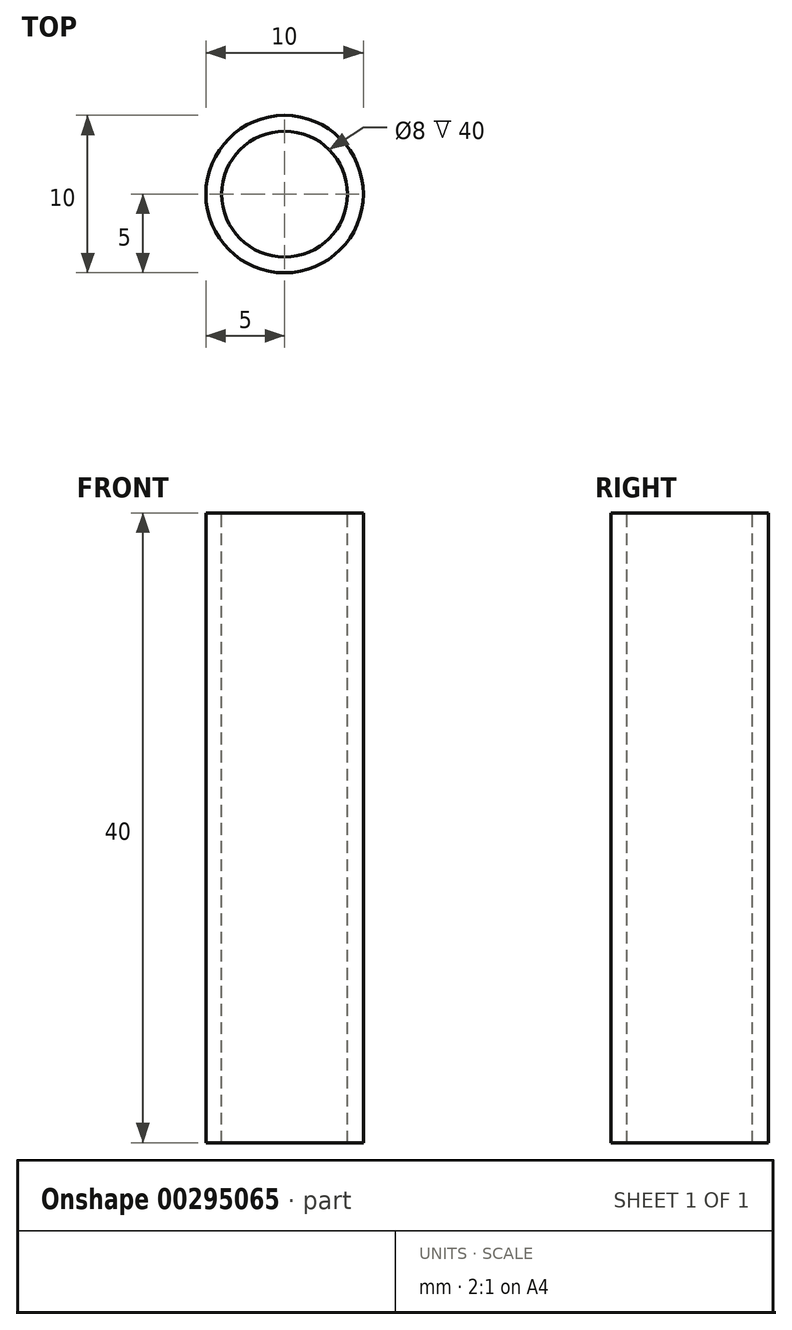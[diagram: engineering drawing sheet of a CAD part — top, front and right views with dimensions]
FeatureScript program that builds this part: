
annotation { "Feature Type Name" : "Feature", "Feature Type Description" : "" }
export const myFeature = defineFeature(function(context is Context, id is Id, definition is map)
    precondition{}
    {
        {
            var Q0;
            Q0=qCreatedBy(makeId("Top.planeOp"),FACE);
            var sketch = newSketch(context, id + "F0", { "sketchPlane" : qUnion([Q0])});
            skCircle(sketch, "E0", {"center": v(0, 0) * mm, "radius": 5 * mm});
            skCircle(sketch, "E1", {"center": v(0, 0) * mm, "radius": 4 * mm});
            skPoint(sketch, "E2", {"position": v(-4, 0) * mm});
            skPoint(sketch, "E3", {"position": v(-5, 0) * mm});
            skSolve(sketch);
        }
        {
            var Q0;
            Q0=makeQuery(id+"F0.imprint","IMPRINT",FACE,{"disambiguationData":[TD([[makeQuery(id+"F0.imprint","IMPRINT",EDGE,{"derivedFrom":sQuery(id+"F0.wireOp",EDGE,"E0")}),1.0]])]});
            extrude(context, id + "F1", {"entities" : qUnion([Q0]), "oppositeDirection" : true, "depth" : 40 * mm});
        }
    });
